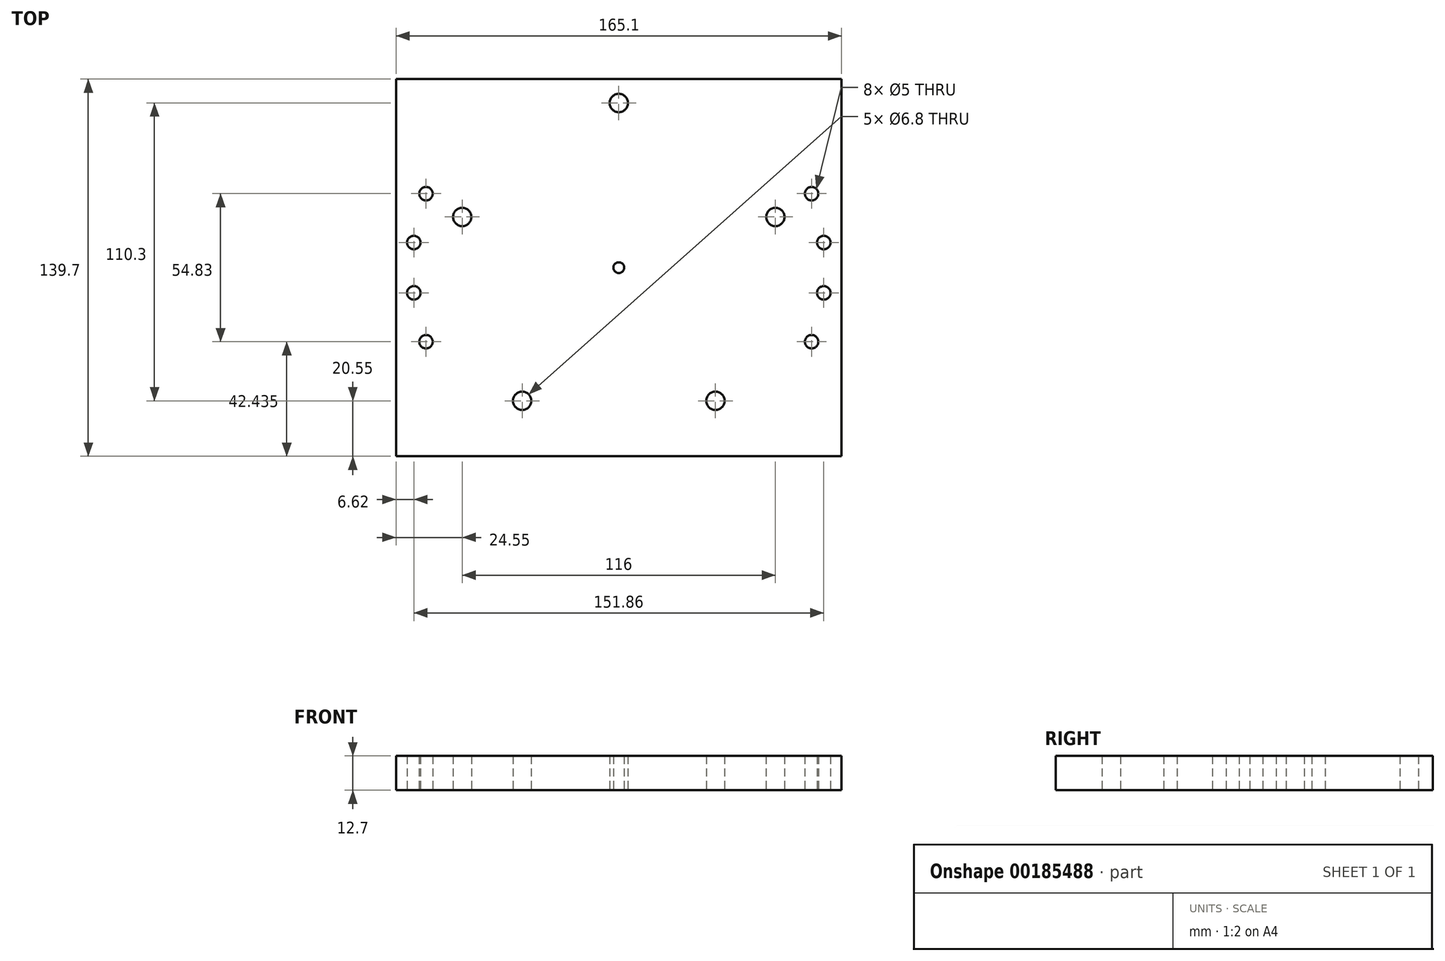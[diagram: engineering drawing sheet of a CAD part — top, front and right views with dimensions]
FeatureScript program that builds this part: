
annotation { "Feature Type Name" : "Feature", "Feature Type Description" : "" }
export const myFeature = defineFeature(function(context is Context, id is Id, definition is map)
    precondition{}
    {
        {
            var Q0;
            Q0=qCreatedBy(makeId("Top.planeOp"),FACE);
            var sketch = newSketch(context, id + "F0", { "sketchPlane" : qUnion([Q0])});
            skPoint(sketch, "E0", {"position": v(0, 61) * mm});
            skPoint(sketch, "E1", {"position": v(58, 18.8) * mm});
            skPoint(sketch, "E2", {"position": v(-58, 18.8) * mm});
            skPoint(sketch, "E3", {"position": v(-35.8, -49.3) * mm});
            skPoint(sketch, "E4", {"position": v(35.8, -49.3) * mm});
            skCircle(sketch, "E5", {"center": v(0, 0) * mm, "radius": 76.5 * mm, "construction": true});
            skLineSegment(sketch, "E6", {"start": v(-106.09, 0) * mm, "end": v(108.78, 0) * mm, "construction": true});
            skLineSegment(sketch, "E7", {"start": v(-75.93, -9.32) * mm, "end": v(0, 0) * mm, "construction": true});
            skLineSegment(sketch, "E8", {"start": v(0, 0) * mm, "end": v(-71.42, -27.42) * mm, "construction": true});
            skPoint(sketch, "E9", {"position": v(-75.93, -9.32) * mm});
            skPoint(sketch, "E10", {"position": v(-71.42, -27.42) * mm});
            skPoint(sketch, "E11.MirrorP", {"position": v(-71.42, 27.42) * mm});
            skPoint(sketch, "E12.MirrorP", {"position": v(-75.93, 9.32) * mm});
            skLineSegment(sketch, "E13", {"start": v(0, 103.09) * mm, "end": v(0, -120.96) * mm, "construction": true});
            skPoint(sketch, "E14.MirrorP", {"position": v(71.42, -27.42) * mm});
            skPoint(sketch, "E15.MirrorP", {"position": v(75.93, -9.32) * mm});
            skPoint(sketch, "E16.MirrorP", {"position": v(75.93, 9.32) * mm});
            skPoint(sketch, "E17.MirrorP", {"position": v(71.42, 27.42) * mm});
            skLineSegment(sketch, "E18.bottom", {"start": v(82.55, -69.85) * mm, "end": v(-82.55, -69.85) * mm});
            skLineSegment(sketch, "E18.top", {"start": v(82.55, 69.85) * mm, "end": v(-82.55, 69.85) * mm});
            skLineSegment(sketch, "E18.left", {"start": v(82.55, -69.85) * mm, "end": v(82.55, 69.85) * mm});
            skLineSegment(sketch, "E18.right", {"start": v(-82.55, -69.85) * mm, "end": v(-82.55, 69.85) * mm});
            skSolve(sketch);
        }
        {
            var Q0;
            Q0=makeQuery(id+"F0.imprint","IMPRINT",FACE,{"disambiguationData":[TD([[makeQuery(id+"F0.imprint","IMPRINT",EDGE,{"derivedFrom":sQuery(id+"F0.wireOp",EDGE,"E18.bottom")}),-1.0]])]});
            extrude(context, id + "F1", {"entities" : qUnion([Q0]), "offsetDistance" : 25 * mm, "depth" : 12.7 * mm});
        }
        {
            var Q0;
            Q0=sQuery(id+"F0.wireOp",VERTEX,"E2");
            var Q1;
            Q1=sQuery(id+"F0.wireOp",VERTEX,"E0");
            var Q2;
            Q2=sQuery(id+"F0.wireOp",VERTEX,"E1");
            var Q3;
            Q3=sQuery(id+"F0.wireOp",VERTEX,"E4");
            var Q4;
            Q4=sQuery(id+"F0.wireOp",VERTEX,"E3");
            var Q5;
            Q5=makeQuery(id+"F1.opExtrude","SWEPT_BODY",BODY,{"disambiguationData":[OSD([sQuery(id+"F0.wireOp",EDGE,"00MS0xD2-BHNz-j4yk-UBuz-BLGiTpOSC9UT")])]});
            var Q6;
            Q6=makeQuery(id+"F1.opExtrude","SWEPT_BODY",BODY,{"disambiguationData":[OSD([sQuery(id+"F0.wireOp",EDGE,"E18.bottom"),sQuery(id+"F0.wireOp",EDGE,"E18.top"),sQuery(id+"F0.wireOp",EDGE,"E18.left"),sQuery(id+"F0.wireOp",EDGE,"E18.right")])]});
            hole(context, id + "F2", {"style" : HoleStyle.SIMPLE, "endStyle" : HoleEndStyle.THROUGH, "oppositeDirection" : true, "standardTappedOrClearance" : lookupTablePath({ "standard" : "ISO", "engagement" : "75%", "pitch" : "1.25 mm", "size" : "M8", "type" : "Tapped" }), "standardBlindInLast" : lookupTablePath({ "standard" : "ISO", "engagement" : "75%", "pitch" : "1.25 mm", "size" : "M8", "type" : "Tapped" }), "holeDiameter" : 6.8 * mm, "startFromSketch" : true, "locations" : qUnion([Q0, Q1, Q2, Q3, Q4]), "scope" : qUnion([Q5, Q6]), "isTappedThrough" : true, "tappedDepth" : 12 * mm, "tapClearance" : 3, "majorDiameter" : 8 * mm, "showTappedDepth" : true});
        }
        {
            var Q0;
            Q0=sQuery(id+"F0.wireOp",VERTEX,"E10");
            var Q1;
            Q1=sQuery(id+"F0.wireOp",VERTEX,"E9");
            var Q2;
            Q2=sQuery(id+"F0.wireOp",VERTEX,"E12.MirrorP");
            var Q3;
            Q3=sQuery(id+"F0.wireOp",VERTEX,"E11.MirrorP");
            var Q4;
            Q4=sQuery(id+"F0.wireOp",VERTEX,"E14.MirrorP");
            var Q5;
            Q5=sQuery(id+"F0.wireOp",VERTEX,"E15.MirrorP");
            var Q6;
            Q6=sQuery(id+"F0.wireOp",VERTEX,"E16.MirrorP");
            var Q7;
            Q7=sQuery(id+"F0.wireOp",VERTEX,"E17.MirrorP");
            var Q8;
            Q8=makeQuery(id+"F1.opExtrude","SWEPT_BODY",BODY,{"disambiguationData":[OSD([sQuery(id+"F0.wireOp",EDGE,"E18.bottom"),sQuery(id+"F0.wireOp",EDGE,"E18.top"),sQuery(id+"F0.wireOp",EDGE,"E18.left"),sQuery(id+"F0.wireOp",EDGE,"E18.right")])]});
            hole(context, id + "F3", {"style" : HoleStyle.SIMPLE, "endStyle" : HoleEndStyle.THROUGH, "oppositeDirection" : true, "standardTappedOrClearance" : lookupTablePath({ "standard" : "ISO", "engagement" : "75%", "pitch" : "1 mm", "size" : "M6", "type" : "Tapped" }), "standardBlindInLast" : lookupTablePath({ "standard" : "ISO", "fit" : "Normal", "engagement" : "75%", "pitch" : "1 mm", "size" : "M6", "type" : "Clearance & tapped" }), "holeDiameter" : 5 * mm, "majorDiameter" : 6 * mm, "showTappedDepth" : true, "isTappedThrough" : true, "tappedDepth" : 12 * mm, "tapClearance" : 3, "startFromSketch" : true, "locations" : qUnion([Q0, Q1, Q2, Q3, Q4, Q5, Q6, Q7]), "scope" : qUnion([Q8])});
        }
        {
            var Q0;
            Q0=sQuery(id+"F0.wireOp",VERTEX,"E5.center");
            var Q1;
            Q1=makeQuery(id+"F1.opExtrude","SWEPT_BODY",BODY,{"disambiguationData":[OSD([sQuery(id+"F0.wireOp",EDGE,"E18.bottom"),sQuery(id+"F0.wireOp",EDGE,"E18.top"),sQuery(id+"F0.wireOp",EDGE,"E18.left"),sQuery(id+"F0.wireOp",EDGE,"E18.right")])]});
            hole(context, id + "F4", {"style" : HoleStyle.SIMPLE, "endStyle" : HoleEndStyle.THROUGH, "oppositeDirection" : true, "standardTappedOrClearance" : lookupTablePath({ "standard" : "ISO", "size" : "4", "type" : "Drilled" }), "standardBlindInLast" : lookupTablePath({ "standard" : "ISO", "size" : "4", "type" : "Drilled" }), "holeDiameter" : 4 * mm, "majorDiameter" : 5 * mm, "isTappedThrough" : true, "tappedDepth" : 12 * mm, "tapClearance" : 3, "startFromSketch" : true, "locations" : qUnion([Q0]), "scope" : qUnion([Q1])});
        }
    });
